# Revit family: AVP Actuator_Flow_PN25_RFA_1
name_source: partatom
category: Pipe Accessories
units: mm (PartAtom-declared; Revit-internal decimal feet)

## family parameters
Always vertical = Yes
Cut with Voids When Loaded = No
OmniClass Number = 23.75.65.14.14.17
OmniClass Title = Flow Controls
Part Type = Normal
Round Connector Dimension = Use Diameter
Shared = No
Work Plane-Based = No

## types (2) — shared parameters
Actuator size = 54.0 cm²
Body Material = Danfoss Stainless Steel
Description = Spring Actuator
Manufacturer = Danfoss
Nominal Pressure = PN 25
URL = https://store.danfoss.com

## per-type parameters (varying)
| type | Differential Pressure Setting Range | Model | Model Type | Spring Colour |
| AVP Actuator_Flow_PN25_dP0.3-2.0bar_003H6835 | 0.3-2.0 bar | 003H6835 | AVP Actuator_Flow_PN25_dP0.3-2.0bar | Danfoss Steel Paint Red (Spring) |
| AVP Actuator_Flow_PN25_dP0.2-1.0bar_003H6834 | 0.2-1.0 bar | 003H6834 | AVP Actuator_Flow_PN25_dP0.2-1.0bar | Danfoss Steel Paint Yellow (Spring) |

## geometry (parser evidence)
native form markers: Sweep x2
no freeform markers — native parametric forms only
